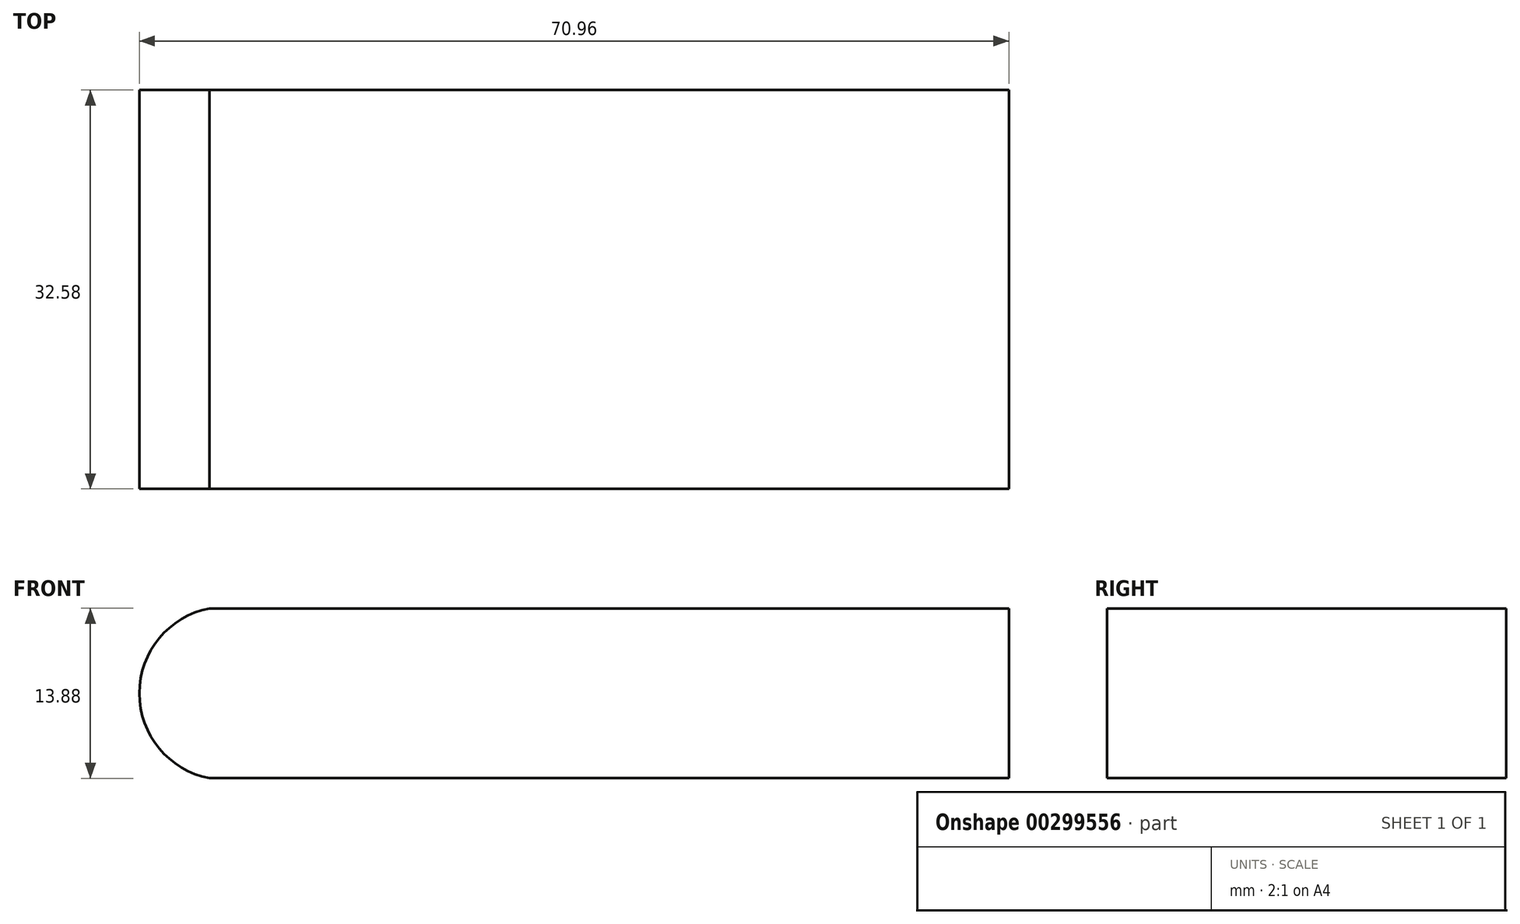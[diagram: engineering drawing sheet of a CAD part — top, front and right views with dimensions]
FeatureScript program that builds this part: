
annotation { "Feature Type Name" : "Feature", "Feature Type Description" : "" }
export const myFeature = defineFeature(function(context is Context, id is Id, definition is map)
    precondition{}
    {
        {
            var Q0;
            Q0=qCreatedBy(makeId("Front.planeOp"),FACE);
            var sketch = newSketch(context, id + "F0", { "sketchPlane" : qUnion([Q0])});
            skLineSegment(sketch, "E0.bottom", {"start": v(35.48, -6.94) * mm, "end": v(-35.48, -6.94) * mm});
            skLineSegment(sketch, "E0.top", {"start": v(35.47, 6.93) * mm, "end": v(-35.48, 6.93) * mm});
            skLineSegment(sketch, "E0.left", {"start": v(35.48, -6.94) * mm, "end": v(35.48, 6.93) * mm});
            skLineSegment(sketch, "E0.right", {"start": v(-35.47, -6.94) * mm, "end": v(-35.48, 6.93) * mm});
            skPoint(sketch, "E0.middle", {"position": v(0, 0) * mm});
            skLineSegment(sketch, "E1", {"start": v(-29.76, 6.93) * mm, "end": v(-29.76, -6.94) * mm, "construction": true});
            skPoint(sketch, "E2", {"position": v(-35.48, 0) * mm});
            skArc(sketch, "E3", {"start": v(-29.76, 6.93) * mm, "mid": v(-35.48, 0) * mm, "end": v(-29.76, -6.94) * mm});
            skSolve(sketch);
        }
        {
            var Q0;
            {var subQ4=sQuery(id+"F0.wireOp",EDGE,"E0.left");Q0=makeQuery(id+"F0.imprint","IMPRINT",FACE,{"disambiguationData":[TD([[makeQuery(id+"F0.imprint","IMPRINT",EDGE,{"derivedFrom":subQ4}),1.0]])]});}
            extrude(context, id + "F1", {"entities" : qUnion([Q0]), "endBound" : BoundingType.SYMMETRIC, "depth" : 32.58 * mm});
        }
    });
